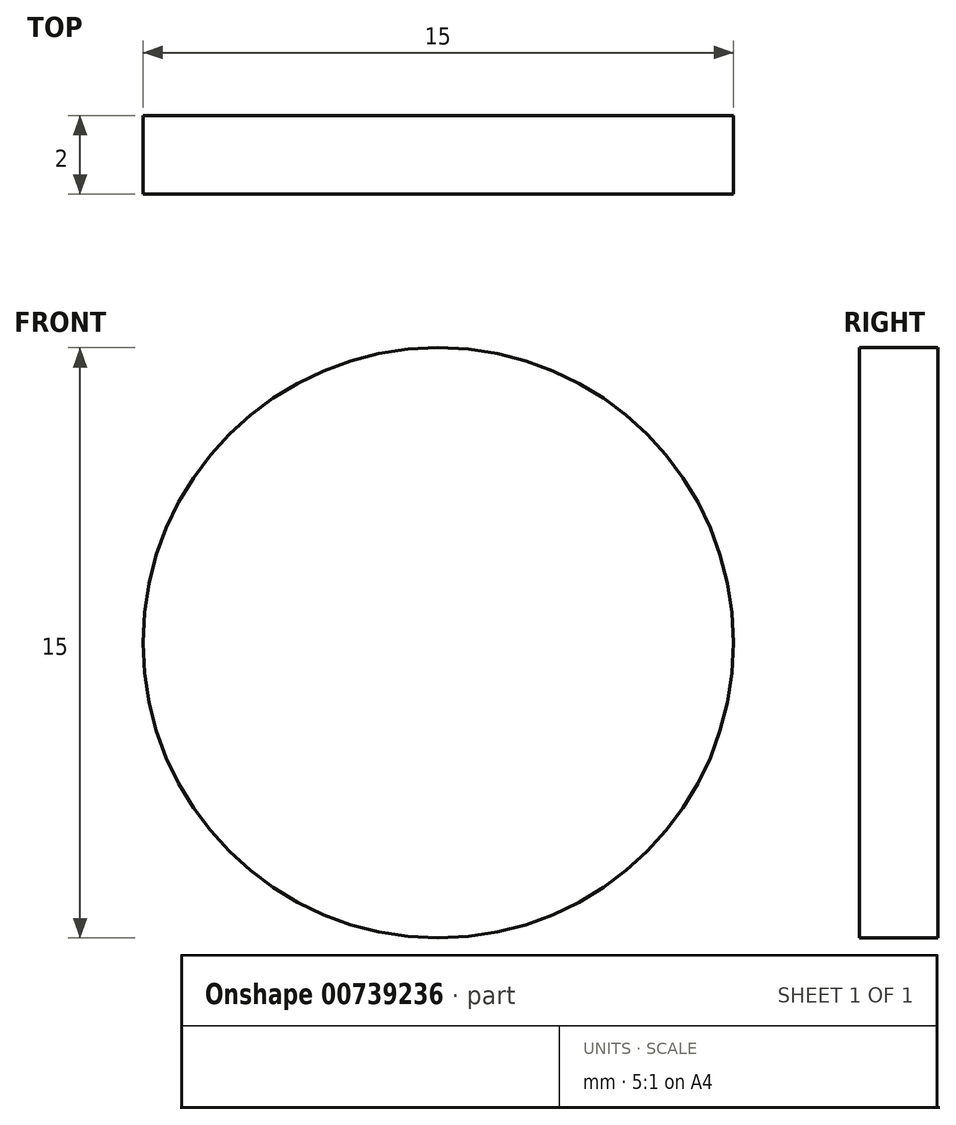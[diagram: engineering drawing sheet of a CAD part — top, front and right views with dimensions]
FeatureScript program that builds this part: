
annotation { "Feature Type Name" : "Feature", "Feature Type Description" : "" }
export const myFeature = defineFeature(function(context is Context, id is Id, definition is map)
    precondition{}
    {
        {
            var Q0;
            Q0=qCreatedBy(makeId("Front.planeOp"),FACE);
            var sketch = newSketch(context, id + "F0", { "sketchPlane" : qUnion([Q0])});
            skCircle(sketch, "E0", {"center": v(0, 0) * mm, "radius": 7.5 * mm});
            skSolve(sketch);
        }
        {
            var Q0;
            Q0 = qSketchRegion(id + "F0", true);
            extrude(context, id + "F1", {"entities" : qUnion([Q0]), "depth" : 2 * mm, "offsetDistance" : 25.4 * mm});
        }
    });
